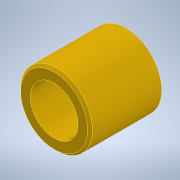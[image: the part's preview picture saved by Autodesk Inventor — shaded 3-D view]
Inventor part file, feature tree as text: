
AUTODESK INVENTOR PART (.ipt)
format: ipt  version: 2022 (Build 260153000, 153)  size: 105,472 bytes
history: native  units: in
note: dims shown in document units (in); Inventor stores cm internally (conversion verified against a paired STEP export)
features: extrude x1, chamfer x1, sketch x1
ambient origin geometry x8: Origin, YZ Plane, XZ Plane, XY Plane, X Axis, Y Axis, Z Axis, Center Point
bodies: Solid1 (feature_tree)
feature tree (3):
  extrude  "Extrusion1"  Depth=1.1811in
  chamfer  "Chamfer1"  Distance=1.1811in
  sketch  "Sketch1"  dims[d0=1.1811in d1=0.7874in d2=1.1811in d3=0.0in d4=0.0394in d5=0.0787in d6=45.0deg]
